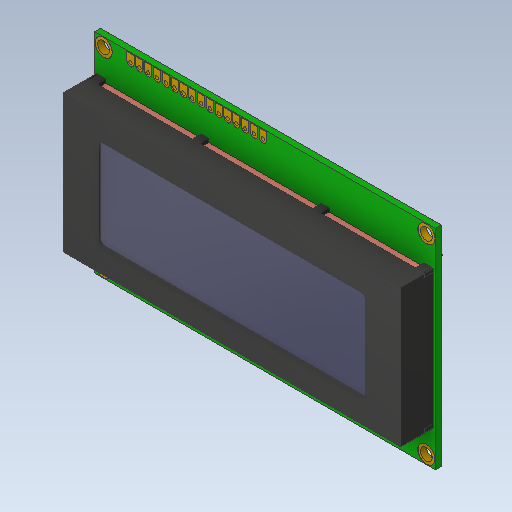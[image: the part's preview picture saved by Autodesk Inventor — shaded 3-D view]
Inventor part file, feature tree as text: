
AUTODESK INVENTOR PART (.ipt)
format: ipt  version: 2020 (Build 240168000, 168)  size: 616,960 bytes
history: native  units: in
note: dims shown in document units (in); Inventor stores cm internally (conversion verified against a paired STEP export)
features: sketch x10, extrude x8, projected_geometry x6, mirror x3, hole x2, fillet x2
ambient origin geometry x8: Origin, YZ Plane, XZ Plane, XY Plane, X Axis, Y Axis, Z Axis, Center Point
bodies: Solid1 (feature_tree)
feature tree (31):
  extrude  "Extrusion1"  Depth=2.371in
  extrude  "Extrusion2"  Depth=0.066in
  mirror  "Mirror1"
  hole  "Hole1"  [1 undecoded]
  extrude  "Extrusion3"  Depth=0.082in
  mirror  "Mirror2"
  hole  "Hole2"  [1 undecoded]
  extrude  "Extrusion4"  Depth=0.1in
  extrude  "Extrusion5"  Depth=3.822in
  extrude  "Extrusion6"  Depth=0.372in TaperAngle=0.0deg
  mirror  "Mirror3"
  extrude  "Extrusion7"  Depth=3.03in
  extrude  "Extrusion8"  Depth=1.021in
  fillet  "Fillet1"  Radius=0.05in
  fillet  "Fillet2"  Radius=0.02in
  sketch  "Sketch1"  dims[d0=3.862in d1=2.371in]
  sketch  "Sketch2"  dims[d2=0.066in d3=0.0in d4=3.66in]
  sketch  "Sketch3"  dims[d5=2.165in d6=0.196in]
  projected_geometry  "Projected Loop1"
  projected_geometry  "Projected Loop2"
  projected_geometry  "Projected Loop3"
  projected_geometry  "Projected Loop4"
  sketch  "Sketch4"  dims[d7=0.001in d8=0.0in]
  sketch  "Sketch5"  dims[d9=0.135in d10=0.75in d11=0.375in d12=0.25in d13=0.5635in d14=1.0in d15=0.8108in d16=0.082in]
  projected_geometry  "Projected Loop5"
  sketch  "Sketch6"  dims[d17=0.089in d18=0.365in]
  sketch  "Sketch7"  dims[d19=0.01in d20=6.2992in d22=0.1in d23=0.3937in d25=1.0in]
  sketch  "Sketch8"  dims[d27=0.001in d28=0.0in]
  projected_geometry  "Projected Loop6"
  sketch  "Sketch9"  dims[d29=0.04in d30=0.75in d31=0.375in d32=0.25in d33=0.5635in d34=1.0in d35=0.8108in d36=3.822in]
  sketch  "Sketch10"  dims[d37=1.567in d38=0.372in d39=0.0in d40=3.03in d41=1.021in d42=0.05in d43=0.02in d44=0.0in d45=1.08in d46=1.08in d50=1.277in d52=0.04in d53=0.0in d54=0.1in d56=0.015in d57=0.005in d58=0.005in d59=0.015in d60=0.2in d61=0.034in d62=0.0825in d63=0.369in d64=0.166in d65=0.088in d66=0.376in d67=0.166in d68=0.7874in d70=1.119in d71=0.3937in d73=1.0in d75=0.1in d76=0.0in d77=0.395in d78=0.862in d79=1.22in d80=1.43in d81=0.885in d82=1.75in d83=0.832in d84=0.914in d85=1.266in d86=0.978in d87=0.816in d88=0.054in d89=0.0in d90=0.19in d91=0.19in d93=0.299in]
note: 2 required parameter values undecoded (feature->parameter linkage not recoverable at this tier; creation-order binding heuristic only, values carry confidence <= 0.55)
